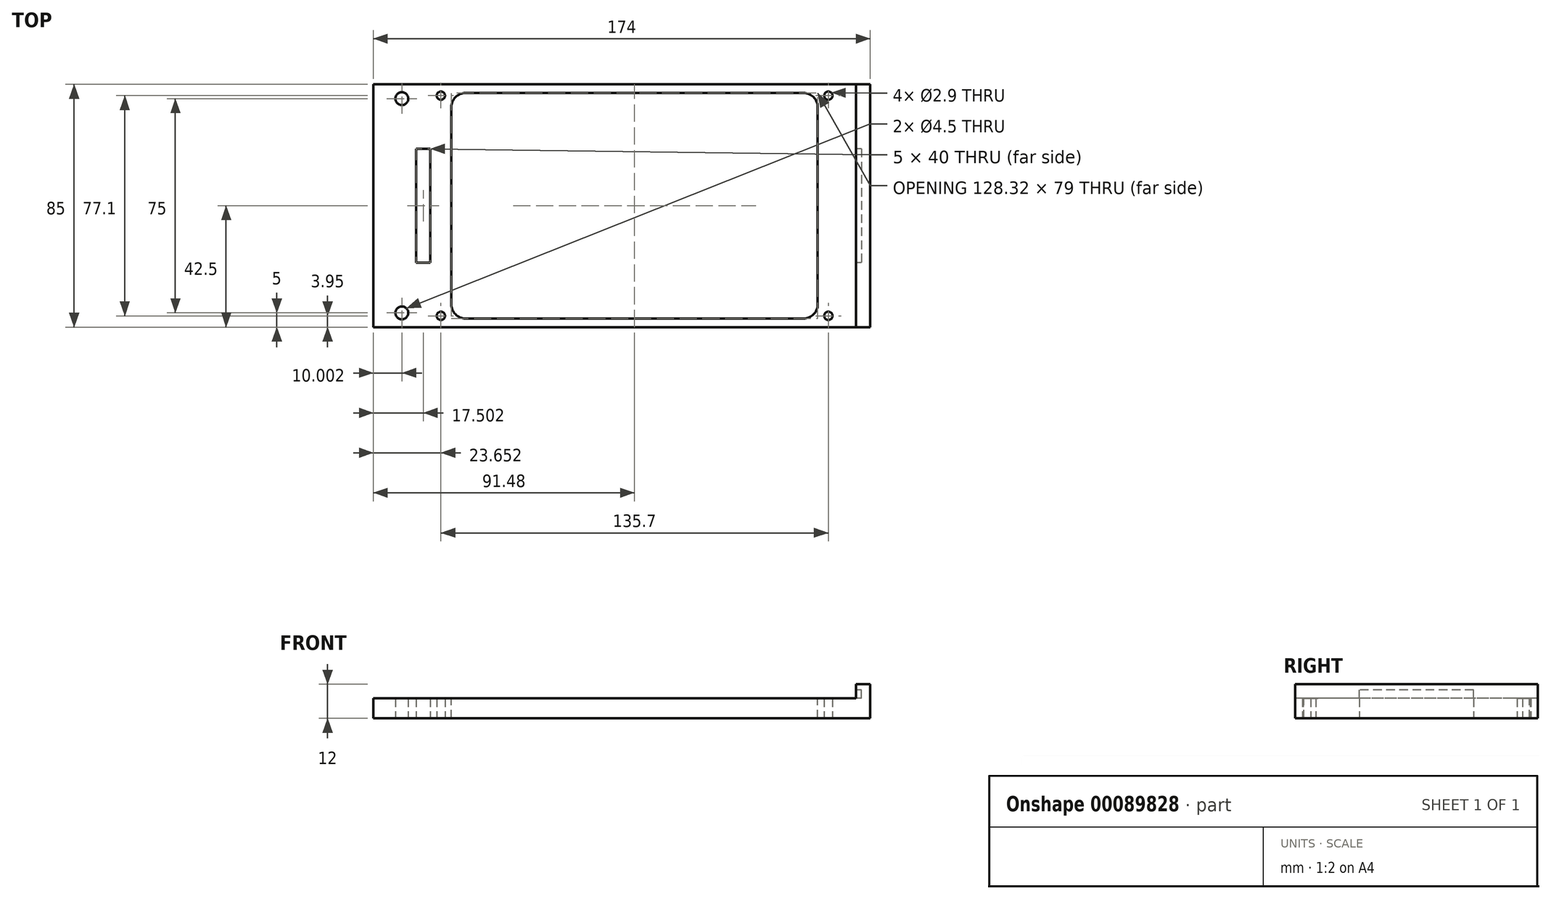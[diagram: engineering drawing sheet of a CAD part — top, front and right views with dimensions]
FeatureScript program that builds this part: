
annotation { "Feature Type Name" : "Feature", "Feature Type Description" : "" }
export const myFeature = defineFeature(function(context is Context, id is Id, definition is map)
    precondition{}
    {
        {
            var Q0;
            Q0=qCreatedBy(makeId("Top.planeOp"),FACE);
            var sketch = newSketch(context, id + "F0", { "sketchPlane" : qUnion([Q0])});
            skLineSegment(sketch, "E0.bottom", {"start": v(-31.79, 0) * mm, "end": v(111.21, 0) * mm});
            skLineSegment(sketch, "E0.top", {"start": v(-31.79, 85) * mm, "end": v(111.21, 85) * mm});
            skLineSegment(sketch, "E0.left", {"start": v(-31.79, 0) * mm, "end": v(-31.79, 85) * mm});
            skLineSegment(sketch, "E0.right", {"start": v(111.21, 0) * mm, "end": v(111.21, 85) * mm});
            skLineSegment(sketch, "E1.bottom", {"start": v(-31.79, 85) * mm, "end": v(-51.79, 85) * mm});
            skLineSegment(sketch, "E1.top", {"start": v(-31.79, 0) * mm, "end": v(-51.79, 0) * mm});
            skLineSegment(sketch, "E1.left", {"start": v(-31.79, 85) * mm, "end": v(-31.79, 0) * mm});
            skLineSegment(sketch, "E1.right", {"start": v(-51.79, 85) * mm, "end": v(-51.79, 0) * mm});
            skLineSegment(sketch, "E2.bottom", {"start": v(111.21, 85) * mm, "end": v(122.21, 85) * mm});
            skLineSegment(sketch, "E2.top", {"start": v(111.21, 0) * mm, "end": v(122.21, 0) * mm});
            skLineSegment(sketch, "E2.left", {"start": v(111.21, 85) * mm, "end": v(111.21, 0) * mm});
            skLineSegment(sketch, "E2.right", {"start": v(122.21, 85) * mm, "end": v(122.21, 0) * mm});
            skCircle(sketch, "E3", {"center": v(-41.79, 80) * mm, "radius": 2.25 * mm});
            skCircle(sketch, "E4", {"center": v(-41.79, 5) * mm, "radius": 2.25 * mm});
            skPoint(sketch, "E5", {"position": v(-41.79, 85) * mm});
            skLineSegment(sketch, "E6", {"start": v(-41.79, 5) * mm, "end": v(-41.79, 0) * mm});
            skLineSegment(sketch, "E7", {"start": v(-41.79, 80) * mm, "end": v(-41.79, 85) * mm});
            skCircle(sketch, "E8", {"center": v(-28.14, 81.05) * mm, "radius": 1.45 * mm});
            skCircle(sketch, "E9", {"center": v(-28.14, 3.95) * mm, "radius": 1.45 * mm});
            skCircle(sketch, "E10", {"center": v(107.56, 81.05) * mm, "radius": 1.45 * mm});
            skCircle(sketch, "E11", {"center": v(107.56, 3.95) * mm, "radius": 1.45 * mm});
            skLineSegment(sketch, "E12", {"start": v(-28.14, 81.05) * mm, "end": v(-31.79, 81.05) * mm});
            skLineSegment(sketch, "E13", {"start": v(-28.14, 81.05) * mm, "end": v(-28.14, 85) * mm});
            skLineSegment(sketch, "E14", {"start": v(107.56, 3.95) * mm, "end": v(107.56, 0) * mm});
            skLineSegment(sketch, "E15", {"start": v(107.56, 3.95) * mm, "end": v(111.21, 3.95) * mm});
            skLineSegment(sketch, "E16.bottom", {"start": v(-31.79, 62.5) * mm, "end": v(-36.79, 62.5) * mm});
            skLineSegment(sketch, "E16.top", {"start": v(-31.79, 22.5) * mm, "end": v(-36.79, 22.5) * mm});
            skLineSegment(sketch, "E16.left", {"start": v(-31.79, 62.5) * mm, "end": v(-31.79, 22.5) * mm});
            skLineSegment(sketch, "E16.right", {"start": v(-36.79, 62.5) * mm, "end": v(-36.79, 22.5) * mm});
            skPoint(sketch, "E17", {"position": v(-51.79, 42.5) * mm});
            skPoint(sketch, "E18", {"position": v(-36.79, 42.5) * mm});
            skLineSegment(sketch, "E19", {"start": v(117.21, 85) * mm, "end": v(117.21, 0) * mm});
            skSolve(sketch);
        }
        {
            var Q0;
            {var subQ0=sQuery(id+"F0.wireOp",EDGE,"E14");var subQ1=sQuery(id+"F0.wireOp",EDGE,"E11");var subQ2=makeQuery(id+"F0.imprint","INTERSECT",VERTEX,{"derivedFrom":[subQ1,subQ0]});Q0=makeQuery(id+"F0.imprint","IMPRINT",FACE,{"disambiguationData":[TD([[makeQuery(id+"F0.imprint","IMPRINT",EDGE,{"disambiguationData":[TD([[subQ2,-1.0]])],"derivedFrom":subQ1}),-1.0]])]});}
            var Q1;
            {var subQ0=sQuery(id+"F0.wireOp",EDGE,"E12");var subQ3=sQuery(id+"F0.wireOp",EDGE,"E8");var subQ4=makeQuery(id+"F0.imprint","INTERSECT",VERTEX,{"derivedFrom":[subQ3,subQ0]});Q1=makeQuery(id+"F0.imprint","IMPRINT",FACE,{"disambiguationData":[TD([[makeQuery(id+"F0.imprint","IMPRINT",EDGE,{"disambiguationData":[TD([[subQ4,1.0]])],"derivedFrom":subQ3}),-1.0]])]});}
            var Q2;
            {var subQ0=sQuery(id+"F0.wireOp",EDGE,"E1.right");Q2=makeQuery(id+"F0.imprint","IMPRINT",FACE,{"disambiguationData":[TD([[makeQuery(id+"F0.imprint","IMPRINT",EDGE,{"derivedFrom":subQ0}),1.0]])]});}
            var Q3;
            Q3=makeQuery(id+"F0.imprint","IMPRINT",FACE,{"disambiguationData":[TD([[makeQuery(id+"F0.imprint","IMPRINT",EDGE,{"derivedFrom":sQuery(id+"F0.wireOp",EDGE,"E9")}),-1.0]])]});
            var Q4;
            {var subQ6=sQuery(id+"F0.wireOp",EDGE,"E19");Q4=makeQuery(id+"F0.imprint","IMPRINT",FACE,{"disambiguationData":[TD([[makeQuery(id+"F0.imprint","IMPRINT",EDGE,{"derivedFrom":subQ6}),-1.0]])]});}
            extrude(context, id + "F1", {"entities" : qUnion([Q0, Q1, Q2, Q3, Q4]), "depth" : 7 * mm});
        }
        {
            var Q0;
            {var subQ3=sQuery(id+"F0.wireOp",EDGE,"E2.bottom");Q0=makeQuery(id+"F0.imprint","IMPRINT",FACE,{"disambiguationData":[TD([[makeQuery(id+"F0.imprint","IMPRINT",EDGE,{"derivedFrom":subQ3}),-1.0]])]});}
            extrude(context, id + "F2", {"entities" : qUnion([Q0]), "operationType" : NewBodyOperationType.ADD, "depth" : 12 * mm});
        }
        {
            var Q0;
            Q0=makeQuery(id+"F2.opExtrude","SWEPT_FACE",FACE,{"disambiguationData":[OSD([sQuery(id+"F0.wireOp",EDGE,"E19")])]});
            var sketch = newSketch(context, id + "F3", { "sketchPlane" : qUnion([Q0])});
            skLineSegment(sketch, "E20.bottom", {"start": v(-62.5, 7) * mm, "end": v(-22.5, 7) * mm});
            skLineSegment(sketch, "E20.top", {"start": v(-62.5, 10) * mm, "end": v(-22.5, 10) * mm});
            skLineSegment(sketch, "E20.left", {"start": v(-62.5, 7) * mm, "end": v(-62.5, 10) * mm});
            skLineSegment(sketch, "E20.right", {"start": v(-22.5, 7) * mm, "end": v(-22.5, 10) * mm});
            skPoint(sketch, "E21", {"position": v(-42.5, 12) * mm});
            skPoint(sketch, "E22", {"position": v(-42.5, 10) * mm});
            skSolve(sketch);
        }
        {
            var Q0;
            Q0=qSketchRegion(id+"F3",true);
            extrude(context, id + "F4", {"entities" : qUnion([Q0]), "operationType" : NewBodyOperationType.REMOVE, "oppositeDirection" : true, "depth" : 2 * mm});
        }
        {
            var Q0;
            Q0=makeQuery(id+"F4.boolean.opBoolean","MERGE",FACE,{"derivedFrom":[makeQuery(id+"F1.opExtrude","CAP_FACE",FACE,{"disambiguationData":[OSD([sQuery(id+"F0.wireOp",EDGE,"E0.bottom"),sQuery(id+"F0.wireOp",EDGE,"E0.top"),sQuery(id+"F0.wireOp",EDGE,"E1.bottom"),sQuery(id+"F0.wireOp",EDGE,"E1.top"),sQuery(id+"F0.wireOp",EDGE,"E1.right"),sQuery(id+"F0.wireOp",EDGE,"E2.bottom"),sQuery(id+"F0.wireOp",EDGE,"E2.top"),sQuery(id+"F0.wireOp",EDGE,"E3"),sQuery(id+"F0.wireOp",EDGE,"E4"),sQuery(id+"F0.wireOp",EDGE,"E8"),sQuery(id+"F0.wireOp",EDGE,"E9"),sQuery(id+"F0.wireOp",EDGE,"E10"),sQuery(id+"F0.wireOp",EDGE,"E11"),sQuery(id+"F0.wireOp",EDGE,"E16.bottom"),sQuery(id+"F0.wireOp",EDGE,"E16.top"),sQuery(id+"F0.wireOp",EDGE,"E16.left"),sQuery(id+"F0.wireOp",EDGE,"E16.right"),sQuery(id+"F0.wireOp",EDGE,"E19")])],"isStart":false}),makeQuery(id+"F4.opExtrude","SWEPT_FACE",FACE,{"disambiguationData":[OSD([sQuery(id+"F3.wireOp",EDGE,"E20.bottom")])]})]});
            var sketch = newSketch(context, id + "F5", { "sketchPlane" : qUnion([Q0])});
            skLineSegment(sketch, "E23.bottom", {"start": v(-24.47, 82) * mm, "end": v(103.85, 82) * mm});
            skLineSegment(sketch, "E23.top", {"start": v(-24.47, 3) * mm, "end": v(103.85, 3) * mm});
            skLineSegment(sketch, "E23.left", {"start": v(-24.47, 82) * mm, "end": v(-24.47, 3) * mm});
            skLineSegment(sketch, "E23.right", {"start": v(103.85, 82) * mm, "end": v(103.85, 3) * mm});
            skSolve(sketch);
        }
        {
            var Q0;
            Q0=qSketchRegion(id+"F5",true);
            extrude(context, id + "F6", {"entities" : qUnion([Q0]), "operationType" : NewBodyOperationType.REMOVE, "oppositeDirection" : true, "depth" : 25 * mm});
        }
        {
            var Q0;
            Q0=makeQuery(id+"F6.boolean.opBoolean","COPY",EDGE,{"derivedFrom":makeQuery(id+"F6.opExtrude","SWEPT_EDGE",EDGE,{"disambiguationData":[OSD([sQuery(id+"F5.wireOp",EDGE,"E23.bottom"),sQuery(id+"F5.wireOp",EDGE,"E23.left")])]})});
            var Q1;
            Q1=makeQuery(id+"F6.boolean.opBoolean","COPY",EDGE,{"derivedFrom":makeQuery(id+"F6.opExtrude","SWEPT_EDGE",EDGE,{"disambiguationData":[OSD([sQuery(id+"F5.wireOp",EDGE,"E23.bottom"),sQuery(id+"F5.wireOp",EDGE,"E23.right")])]})});
            var Q2;
            Q2=makeQuery(id+"F6.boolean.opBoolean","COPY",EDGE,{"derivedFrom":makeQuery(id+"F6.opExtrude","SWEPT_EDGE",EDGE,{"disambiguationData":[OSD([sQuery(id+"F5.wireOp",EDGE,"E23.top"),sQuery(id+"F5.wireOp",EDGE,"E23.right")])]})});
            var Q3;
            Q3=makeQuery(id+"F6.boolean.opBoolean","COPY",EDGE,{"derivedFrom":makeQuery(id+"F6.opExtrude","SWEPT_EDGE",EDGE,{"disambiguationData":[OSD([sQuery(id+"F5.wireOp",EDGE,"E23.top"),sQuery(id+"F5.wireOp",EDGE,"E23.left")])]})});
            fillet(context, id + "F7", {"entities" : qUnion([Q0, Q1, Q2, Q3]), "radius" : 5 * mm, "tangentPropagation" : true, "allowEdgeOverflow" : false});
        }
    });
